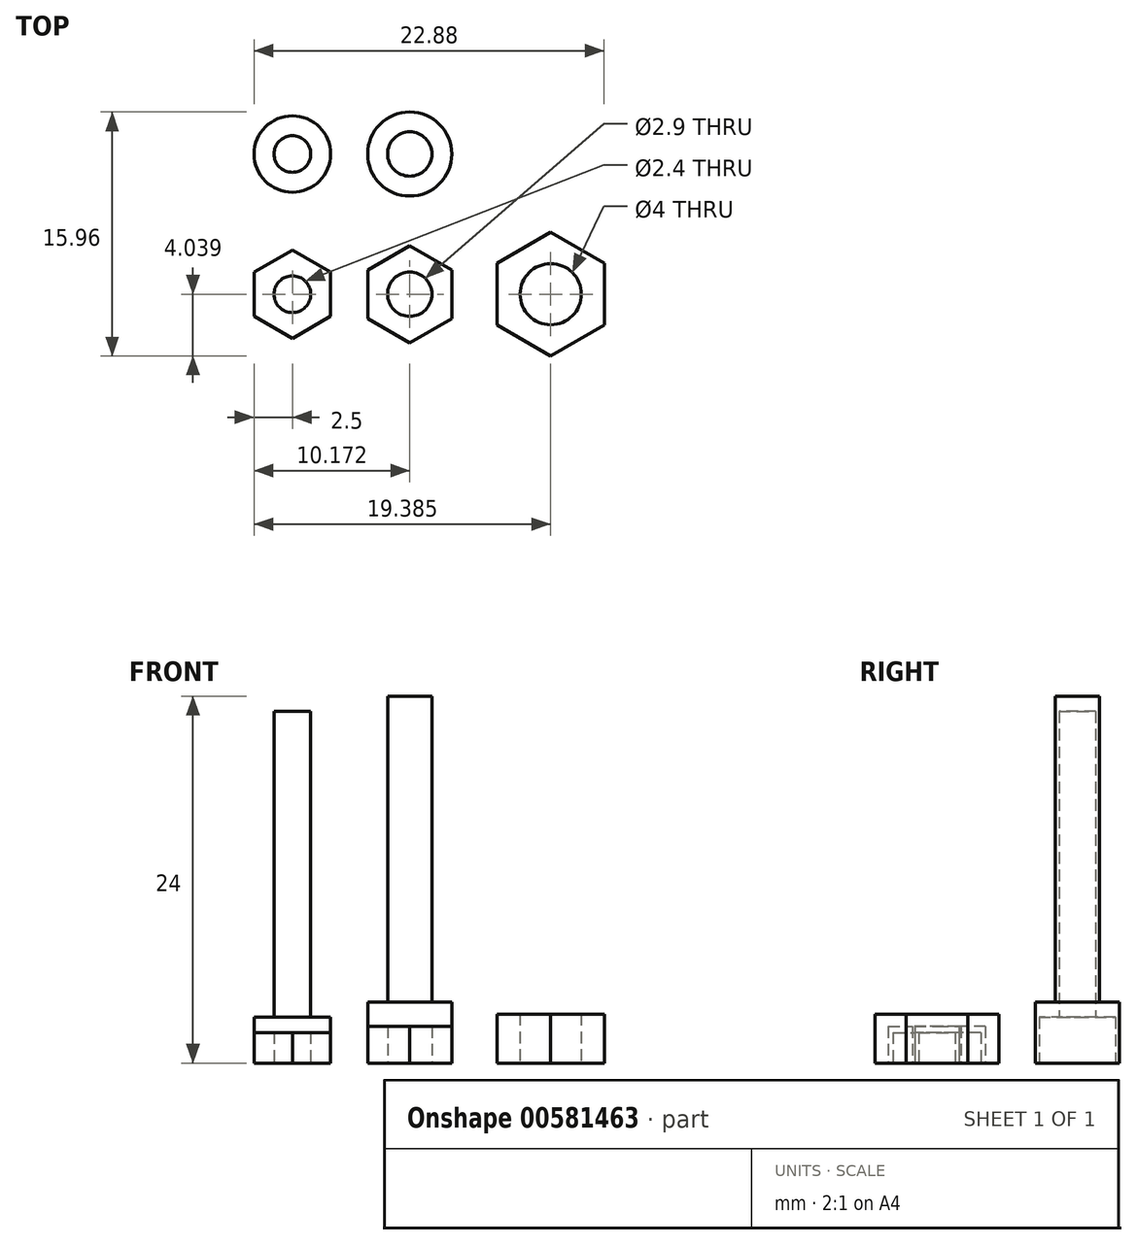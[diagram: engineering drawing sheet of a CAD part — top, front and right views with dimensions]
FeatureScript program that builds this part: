
annotation { "Feature Type Name" : "Feature", "Feature Type Description" : "" }
export const myFeature = defineFeature(function(context is Context, id is Id, definition is map)
    precondition{}
    {
        {
            var Q0;
            Q0=qCreatedBy(makeId("Top.planeOp"),FACE);
            var sketch = newSketch(context, id + "F0", { "sketchPlane" : qUnion([Q0])});
            skCircle(sketch, "E0", {"center": v(0, 0) * mm, "radius": 1.2 * mm});
            skCircle(sketch, "E1.cCircle", {"center": v(0, -9.17) * mm, "radius": 2.5 * mm, "construction": true});
            skLineSegment(sketch, "E1.0", {"start": v(2.5, -7.73) * mm, "end": v(2.5, -10.61) * mm});
            skLineSegment(sketch, "E1.1", {"start": v(2.5, -10.61) * mm, "end": v(0, -12.06) * mm});
            skLineSegment(sketch, "E1.2", {"start": v(0, -12.06) * mm, "end": v(-2.5, -10.61) * mm});
            skLineSegment(sketch, "E1.3", {"start": v(-2.5, -10.61) * mm, "end": v(-2.5, -7.73) * mm});
            skLineSegment(sketch, "E1.4", {"start": v(-2.5, -7.73) * mm, "end": v(0, -6.28) * mm});
            skLineSegment(sketch, "E1.5", {"start": v(0, -6.28) * mm, "end": v(2.5, -7.73) * mm});
            skPoint(sketch, "E1.0.midPoint", {"position": v(2.5, -9.17) * mm});
            skCircle(sketch, "E2", {"center": v(0, -9.17) * mm, "radius": 1.2 * mm});
            skCircle(sketch, "E3", {"center": v(7.67, 0) * mm, "radius": 1.45 * mm});
            skCircle(sketch, "E4", {"center": v(7.67, -9.17) * mm, "radius": 1.45 * mm});
            skCircle(sketch, "E5.cCircle", {"center": v(7.67, -9.17) * mm, "radius": 2.75 * mm, "construction": true});
            skLineSegment(sketch, "E5.0", {"start": v(10.42, -7.58) * mm, "end": v(10.42, -10.76) * mm});
            skLineSegment(sketch, "E5.1", {"start": v(10.42, -10.76) * mm, "end": v(7.67, -12.35) * mm});
            skLineSegment(sketch, "E5.2", {"start": v(7.67, -12.35) * mm, "end": v(4.92, -10.76) * mm});
            skLineSegment(sketch, "E5.3", {"start": v(4.92, -10.76) * mm, "end": v(4.92, -7.58) * mm});
            skLineSegment(sketch, "E5.4", {"start": v(4.92, -7.58) * mm, "end": v(7.67, -6) * mm});
            skLineSegment(sketch, "E5.5", {"start": v(7.67, -6) * mm, "end": v(10.42, -7.58) * mm});
            skPoint(sketch, "E5.0.midPoint", {"position": v(10.42, -9.17) * mm});
            skCircle(sketch, "E6", {"center": v(0, 0) * mm, "radius": 2.5 * mm});
            skCircle(sketch, "E7", {"center": v(7.67, 0) * mm, "radius": 2.75 * mm});
            skCircle(sketch, "E8", {"center": v(16.88, 0) * mm, "radius": 2 * mm});
            skCircle(sketch, "E9.cCircle", {"center": v(16.88, -9.17) * mm, "radius": 3.5 * mm, "construction": true});
            skLineSegment(sketch, "E9.0", {"start": v(20.38, -7.15) * mm, "end": v(20.38, -11.2) * mm});
            skLineSegment(sketch, "E9.1", {"start": v(20.38, -11.2) * mm, "end": v(16.88, -13.21) * mm});
            skLineSegment(sketch, "E9.2", {"start": v(16.88, -13.21) * mm, "end": v(13.38, -11.2) * mm});
            skLineSegment(sketch, "E9.3", {"start": v(13.38, -11.2) * mm, "end": v(13.38, -7.15) * mm});
            skLineSegment(sketch, "E9.4", {"start": v(13.38, -7.15) * mm, "end": v(16.88, -5.13) * mm});
            skLineSegment(sketch, "E9.5", {"start": v(16.88, -5.13) * mm, "end": v(20.38, -7.15) * mm});
            skPoint(sketch, "E9.0.midPoint", {"position": v(20.38, -9.17) * mm});
            skCircle(sketch, "E10", {"center": v(16.88, 0) * mm, "radius": 3.5 * mm});
            skCircle(sketch, "E11", {"center": v(16.88, -9.17) * mm, "radius": 2 * mm});
            skSolve(sketch);
        }
        {
            var Q0;
            Q0=makeQuery(id+"F0.imprint","IMPRINT",FACE,{"disambiguationData":[TD([[makeQuery(id+"F0.imprint","IMPRINT",EDGE,{"derivedFrom":sQuery(id+"F0.wireOp",EDGE,"E1.0")}),-1.0]])]});
            extrude(context, id + "F1", {"entities" : qUnion([Q0]), "depth" : 2 * mm, "offsetDistance" : 25 * mm});
        }
        {
            var Q0;
            Q0=makeQuery(id+"F0.imprint","IMPRINT",FACE,{"disambiguationData":[TD([[makeQuery(id+"F0.imprint","IMPRINT",EDGE,{"derivedFrom":sQuery(id+"F0.wireOp",EDGE,"E0")}),1.0]])]});
            extrude(context, id + "F2", {"entities" : qUnion([Q0]), "depth" : 23 * mm, "offsetDistance" : 25 * mm});
        }
        {
            var Q0;
            Q0=makeQuery(id+"F0.imprint","IMPRINT",FACE,{"disambiguationData":[TD([[makeQuery(id+"F0.imprint","IMPRINT",EDGE,{"derivedFrom":sQuery(id+"F0.wireOp",EDGE,"E0")}),-1.0]])]});
            extrude(context, id + "F3", {"entities" : qUnion([Q0]), "operationType" : NewBodyOperationType.ADD, "depth" : 3 * mm, "offsetDistance" : 25 * mm});
        }
        {
            var Q0;
            Q0=makeQuery(id+"F0.imprint","IMPRINT",FACE,{"disambiguationData":[TD([[makeQuery(id+"F0.imprint","IMPRINT",EDGE,{"derivedFrom":sQuery(id+"F0.wireOp",EDGE,"E4")}),-1.0]])]});
            extrude(context, id + "F4", {"entities" : qUnion([Q0]), "depth" : 2.4 * mm, "offsetDistance" : 25 * mm});
        }
        {
            var Q0;
            Q0=makeQuery(id+"F0.imprint","IMPRINT",FACE,{"disambiguationData":[TD([[makeQuery(id+"F0.imprint","IMPRINT",EDGE,{"derivedFrom":sQuery(id+"F0.wireOp",EDGE,"E3")}),1.0]])]});
            extrude(context, id + "F5", {"entities" : qUnion([Q0]), "depth" : 24 * mm, "offsetDistance" : 25 * mm});
        }
        {
            var Q0;
            Q0=makeQuery(id+"F0.imprint","IMPRINT",FACE,{"disambiguationData":[TD([[makeQuery(id+"F0.imprint","IMPRINT",EDGE,{"derivedFrom":sQuery(id+"F0.wireOp",EDGE,"E3")}),-1.0]])]});
            extrude(context, id + "F6", {"entities" : qUnion([Q0]), "operationType" : NewBodyOperationType.ADD, "depth" : 4 * mm, "offsetDistance" : 25 * mm});
        }
        {
            var Q0;
            Q0=makeQuery(id+"F0.imprint","IMPRINT",FACE,{"disambiguationData":[TD([[makeQuery(id+"F0.imprint","IMPRINT",EDGE,{"derivedFrom":sQuery(id+"F0.wireOp",EDGE,"E9.0")}),-1.0]])]});
            extrude(context, id + "F7", {"entities" : qUnion([Q0]), "depth" : 3.2 * mm, "offsetDistance" : 25 * mm});
        }
    });
